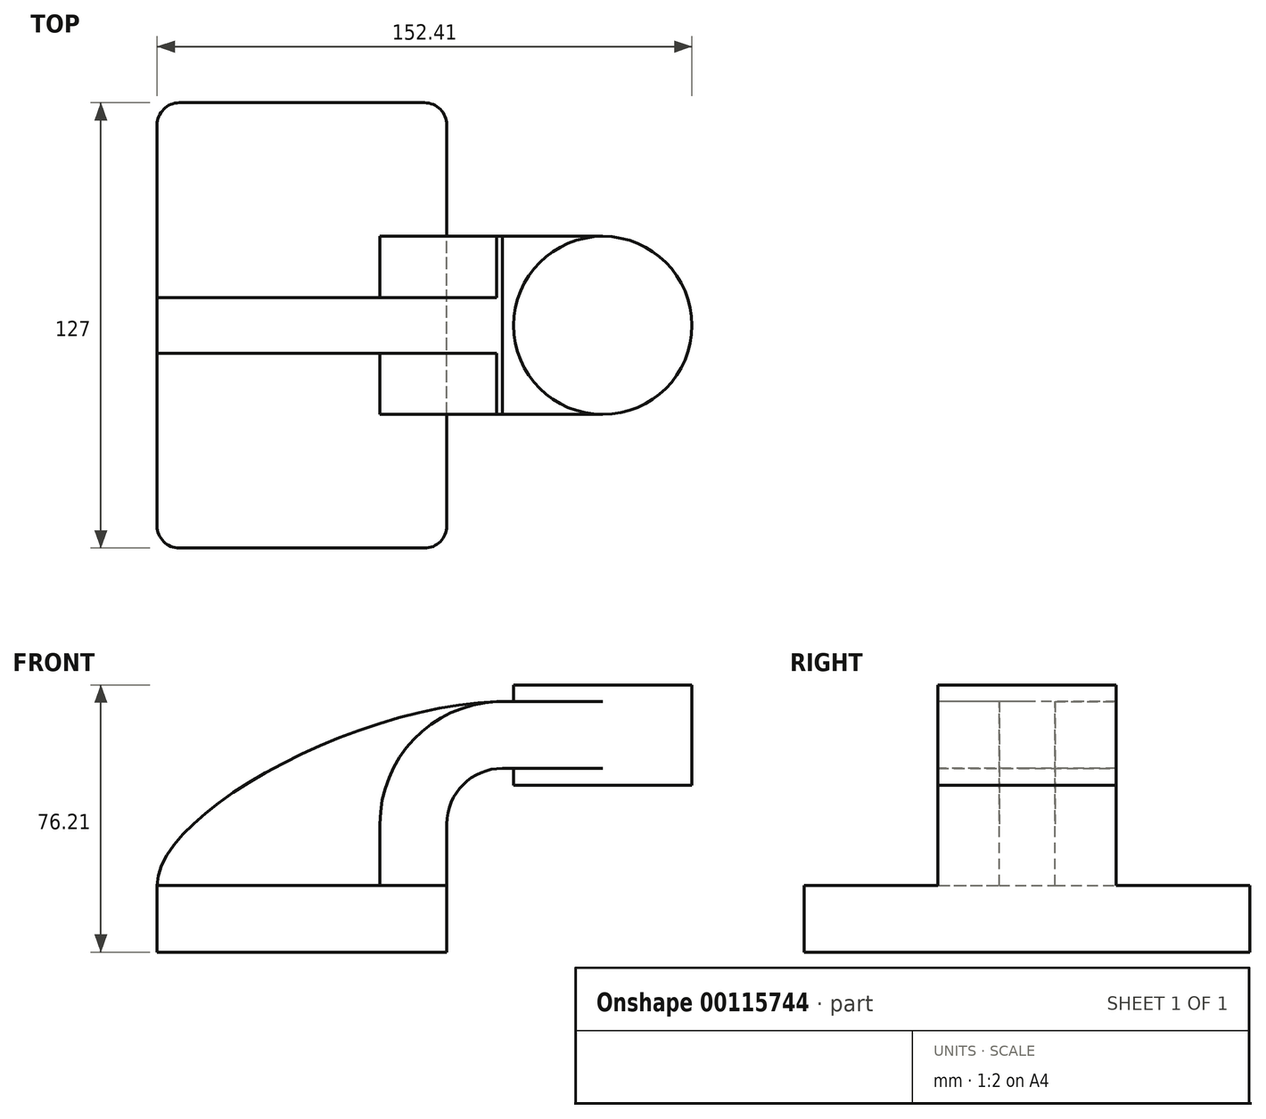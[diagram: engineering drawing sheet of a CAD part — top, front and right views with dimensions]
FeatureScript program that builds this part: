
annotation { "Feature Type Name" : "Feature", "Feature Type Description" : "" }
export const myFeature = defineFeature(function(context is Context, id is Id, definition is map)
    precondition{}
    {
        {
            var Q0;
            Q0=qCreatedBy(makeId("Front.planeOp"),FACE);
            var sketch = newSketch(context, id + "F0", { "sketchPlane" : qUnion([Q0])});
            skLineSegment(sketch, "E0.bottom", {"start": v(-41.28, 9.53) * mm, "end": v(41.28, 9.53) * mm});
            skLineSegment(sketch, "E0.top", {"start": v(-41.28, -9.53) * mm, "end": v(41.28, -9.53) * mm});
            skLineSegment(sketch, "E0.left", {"start": v(-41.28, 9.53) * mm, "end": v(-41.28, -9.53) * mm});
            skLineSegment(sketch, "E0.right", {"start": v(41.28, 9.53) * mm, "end": v(41.28, -9.53) * mm});
            skPoint(sketch, "E0.middle", {"position": v(0, 0) * mm});
            skLineSegment(sketch, "E1.bottom", {"start": v(60.33, 38.1) * mm, "end": v(111.13, 38.1) * mm});
            skLineSegment(sketch, "E1.top", {"start": v(60.33, 66.67) * mm, "end": v(111.13, 66.67) * mm});
            skLineSegment(sketch, "E1.left", {"start": v(60.33, 38.1) * mm, "end": v(60.33, 66.68) * mm});
            skLineSegment(sketch, "E1.right", {"start": v(111.13, 38.1) * mm, "end": v(111.13, 66.67) * mm});
            skPoint(sketch, "E1.middle", {"position": v(85.73, 52.39) * mm});
            skLineSegment(sketch, "E2", {"start": v(41.28, 9.53) * mm, "end": v(41.28, 27) * mm});
            skArc(sketch, "E3", {"start": v(41.28, 27) * mm, "mid": v(45.92, 38.23) * mm, "end": v(57.15, 42.88) * mm});
            skLineSegment(sketch, "E4", {"start": v(57.15, 42.88) * mm, "end": v(85.73, 42.88) * mm});
            skLineSegment(sketch, "E5", {"start": v(85.73, 38.1) * mm, "end": v(85.73, 42.88) * mm, "construction": true});
            skLineSegment(sketch, "E6.0", {"start": v(57.15, 61.93) * mm, "end": v(85.73, 61.93) * mm});
            skArc(sketch, "E6.1", {"start": v(22.23, 27) * mm, "mid": v(32.45, 51.7) * mm, "end": v(57.15, 61.93) * mm});
            skLineSegment(sketch, "E6.2", {"start": v(22.23, 9.53) * mm, "end": v(22.23, 27) * mm});
            skLineSegment(sketch, "E7", {"start": v(85.73, 38.1) * mm, "end": v(85.73, 66.67) * mm});
            skFitSpline(sketch, "E8", {"points": [v(-41.28, 9.53) * mm, v(57.15, 61.93) * mm], "startDerivative": vector(0.95, 63.12) * mm, "endDerivative": vector(121.59, 1.67) * mm});
            skSolve(sketch);
        }
        {
            var Q0;
            Q0=makeQuery(id+"F0.imprint","IMPRINT",FACE,{"disambiguationData":[TD([[makeQuery(id+"F0.imprint","IMPRINT",EDGE,{"derivedFrom":sQuery(id+"F0.wireOp",EDGE,"E0.top")}),1.0]])]});
            extrude(context, id + "F1", {"entities" : qUnion([Q0]), "endBound" : BoundingType.SYMMETRIC, "depth" : 127 * mm});
        }
        {
            var Q0;
            {var subQ1=sQuery(id+"F0.wireOp",EDGE,"E2");Q0=makeQuery(id+"F0.imprint","IMPRINT",FACE,{"disambiguationData":[TD([[makeQuery(id+"F0.imprint","IMPRINT",EDGE,{"derivedFrom":subQ1}),1.0]])]});}
            var Q1;
            {var subQ0=sQuery(id+"F0.wireOp",EDGE,"E4");var subQ1=sQuery(id+"F0.wireOp",EDGE,"E1.left");var subQ2=makeQuery(id+"F0.imprint","INTERSECT",VERTEX,{"derivedFrom":[subQ1,subQ0]});Q1=makeQuery(id+"F0.imprint","IMPRINT",FACE,{"disambiguationData":[TD([[makeQuery(id+"F0.imprint","IMPRINT",EDGE,{"disambiguationData":[TD([[subQ2,-1.0]])],"derivedFrom":subQ1}),-1.0]])]});}
            extrude(context, id + "F2", {"entities" : qUnion([Q0, Q1]), "operationType" : NewBodyOperationType.ADD, "endBound" : BoundingType.SYMMETRIC, "depth" : 50.8 * mm});
        }
        {
            var Q0;
            {var subQ3=sQuery(id+"F0.wireOp",EDGE,"E6.2");Q0=makeQuery(id+"F0.imprint","IMPRINT",FACE,{"disambiguationData":[TD([[makeQuery(id+"F0.imprint","IMPRINT",EDGE,{"derivedFrom":subQ3}),1.0]])]});}
            extrude(context, id + "F3", {"entities" : qUnion([Q0]), "operationType" : NewBodyOperationType.ADD, "endBound" : BoundingType.SYMMETRIC, "depth" : 15.88 * mm});
        }
        {
            var Q0;
            {var subQ0=sQuery(id+"F0.wireOp",EDGE,"E1.right");Q0=makeQuery(id+"F0.imprint","IMPRINT",FACE,{"disambiguationData":[TD([[makeQuery(id+"F0.imprint","IMPRINT",EDGE,{"derivedFrom":subQ0}),1.0]])]});}
            var Q1;
            Q1=sQuery(id+"F0.wireOp",EDGE,"E7");
            revolve(context, id + "F4", {"operationType" : NewBodyOperationType.ADD, "entities" : qUnion([Q0]), "axis" : qUnion([Q1]), "revolveType" : RevolveType.FULL});
        }
        {
            var Q0;
            Q0=makeQuery(id+"F1.opExtrude","CAP_EDGE",EDGE,{"disambiguationData":[OSD([sQuery(id+"F0.wireOp",EDGE,"E0.right")])],"isStart":false});
            var Q1;
            Q1=makeQuery(id+"F1.opExtrude","CAP_EDGE",EDGE,{"disambiguationData":[OSD([sQuery(id+"F0.wireOp",EDGE,"E0.left")])],"isStart":false});
            var Q2;
            Q2=makeQuery(id+"F1.opExtrude","CAP_EDGE",EDGE,{"disambiguationData":[OSD([sQuery(id+"F0.wireOp",EDGE,"E0.right")])],"isStart":true});
            var Q3;
            Q3=makeQuery(id+"F1.opExtrude","CAP_EDGE",EDGE,{"disambiguationData":[OSD([sQuery(id+"F0.wireOp",EDGE,"E0.left")])],"isStart":true});
            fillet(context, id + "F5", {"entities" : qUnion([Q0, Q1, Q2, Q3]), "radius" : 6.35 * mm, "tangentPropagation" : true, "allowEdgeOverflow" : false});
        }
    });
